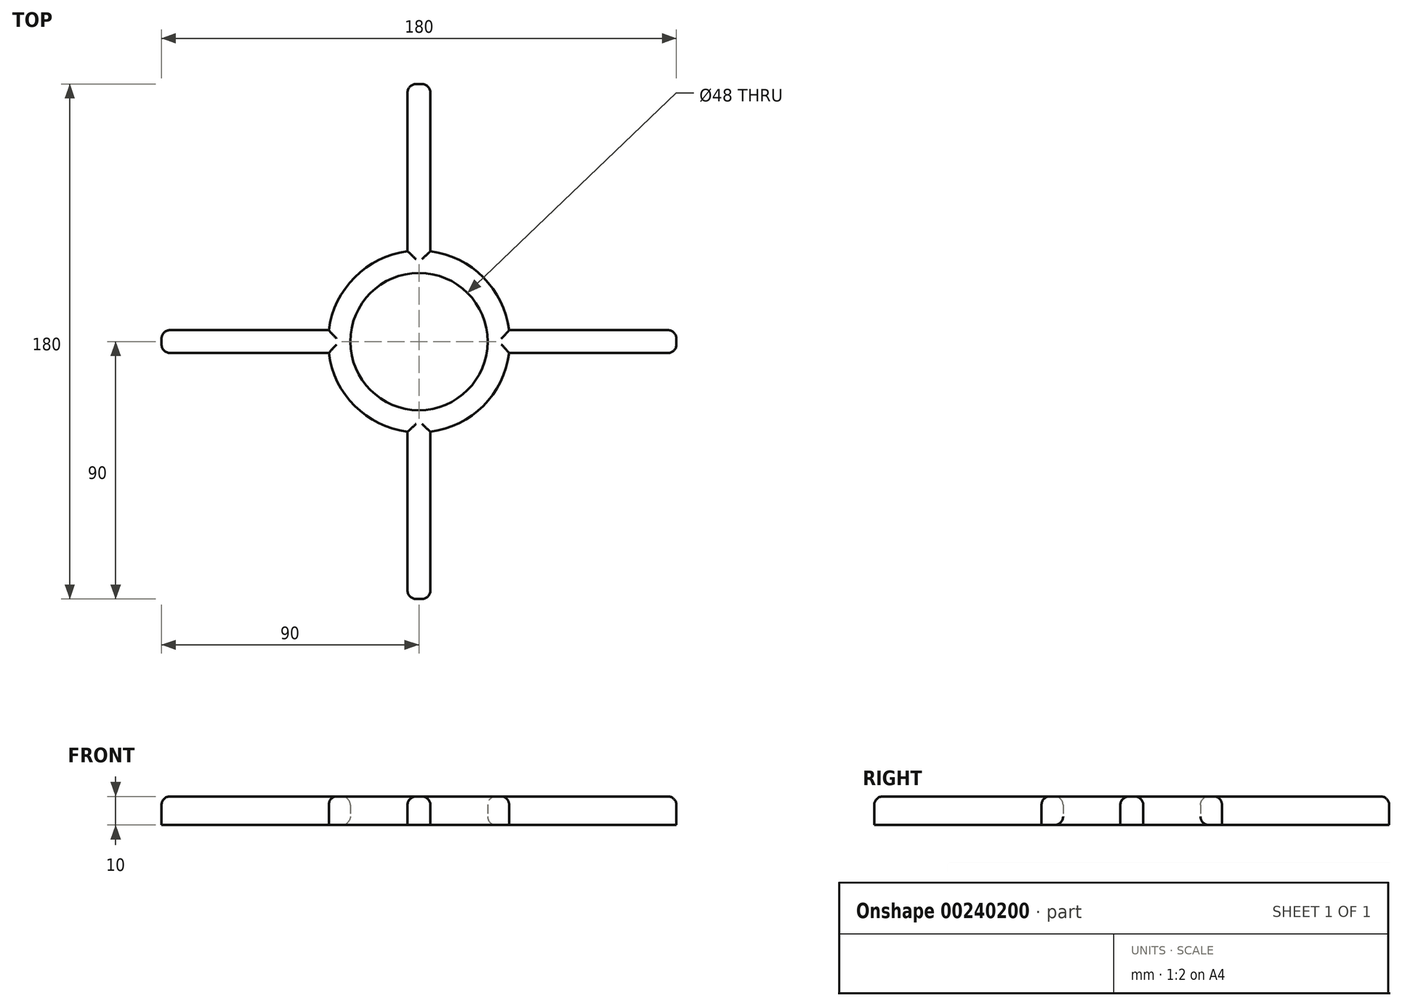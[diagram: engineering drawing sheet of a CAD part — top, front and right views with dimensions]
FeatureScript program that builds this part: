
annotation { "Feature Type Name" : "Feature", "Feature Type Description" : "" }
export const myFeature = defineFeature(function(context is Context, id is Id, definition is map)
    precondition{}
    {
        {
            var Q0;
            Q0=qCreatedBy(makeId("Top.planeOp"),FACE);
            var sketch = newSketch(context, id + "F0", { "sketchPlane" : qUnion([Q0])});
            skLineSegment(sketch, "E0.bottom", {"start": v(90, -4) * mm, "end": v(31.53, -4) * mm});
            skLineSegment(sketch, "E0.top", {"start": v(90, 4) * mm, "end": v(31.53, 4) * mm});
            skLineSegment(sketch, "E0.left", {"start": v(90, -4) * mm, "end": v(90, 4) * mm});
            skLineSegment(sketch, "E0.right", {"start": v(-90, -4) * mm, "end": v(-90, 4) * mm});
            skPoint(sketch, "E0.middle", {"position": v(0, 0) * mm});
            skCircle(sketch, "E1", {"center": v(0, 0) * mm, "radius": 24 * mm});
            skArc(sketch, "E2", {"start": v(-31.53, -4) * mm, "mid": v(-22.47, -22.47) * mm, "end": v(-4, -31.53) * mm});
            skArc(sketch, "E3.trimOffspring", {"start": v(31.53, 4) * mm, "mid": v(22.47, 22.47) * mm, "end": v(4, 31.53) * mm});
            skLineSegment(sketch, "E4.trimOffspring", {"start": v(-31.53, -4) * mm, "end": v(-90, -4) * mm});
            skLineSegment(sketch, "E5.trimOffspring", {"start": v(-31.53, 4) * mm, "end": v(-90, 4) * mm});
            skLineSegment(sketch, "E6.bottom", {"start": v(-4, 90) * mm, "end": v(4, 90) * mm});
            skLineSegment(sketch, "E6.top", {"start": v(-4, -90) * mm, "end": v(4, -90) * mm});
            skLineSegment(sketch, "E6.left", {"start": v(-4, 90) * mm, "end": v(-4, 31.53) * mm});
            skLineSegment(sketch, "E6.right", {"start": v(4, 90) * mm, "end": v(4, 31.53) * mm});
            skLineSegment(sketch, "E7.trimOffspring", {"start": v(-4, -31.53) * mm, "end": v(-4, -90) * mm});
            skLineSegment(sketch, "E8.trimOffspring", {"start": v(4, -31.53) * mm, "end": v(4, -90) * mm});
            skArc(sketch, "E9.trimOffspring", {"start": v(4, -31.53) * mm, "mid": v(22.47, -22.47) * mm, "end": v(31.53, -4) * mm});
            skArc(sketch, "E10.trimOffspring", {"start": v(-4, 31.53) * mm, "mid": v(-22.47, 22.47) * mm, "end": v(-31.53, 4) * mm});
            skSolve(sketch);
        }
        {
            var Q0;
            Q0=makeQuery(id+"F0.imprint","IMPRINT",FACE,{"disambiguationData":[TD([[makeQuery(id+"F0.imprint","IMPRINT",EDGE,{"derivedFrom":sQuery(id+"F0.wireOp",EDGE,"E0.bottom")}),-1.0]])]});
            extrude(context, id + "F1", {"entities" : qUnion([Q0]), "depth" : 10 * mm});
        }
        {
            var Q0;
            Q0=makeQuery(id+"F1.opExtrude","CAP_FACE",FACE,{"disambiguationData":[OSD([sQuery(id+"F0.wireOp",EDGE,"E0.bottom"),sQuery(id+"F0.wireOp",EDGE,"E0.top"),sQuery(id+"F0.wireOp",EDGE,"E0.left"),sQuery(id+"F0.wireOp",EDGE,"E0.right"),sQuery(id+"F0.wireOp",EDGE,"E1"),sQuery(id+"F0.wireOp",EDGE,"E2"),sQuery(id+"F0.wireOp",EDGE,"E3.trimOffspring"),sQuery(id+"F0.wireOp",EDGE,"E4.trimOffspring"),sQuery(id+"F0.wireOp",EDGE,"E5.trimOffspring"),sQuery(id+"F0.wireOp",EDGE,"E6.bottom"),sQuery(id+"F0.wireOp",EDGE,"E6.top"),sQuery(id+"F0.wireOp",EDGE,"E6.left"),sQuery(id+"F0.wireOp",EDGE,"E6.right"),sQuery(id+"F0.wireOp",EDGE,"E7.trimOffspring"),sQuery(id+"F0.wireOp",EDGE,"E8.trimOffspring"),sQuery(id+"F0.wireOp",EDGE,"E9.trimOffspring"),sQuery(id+"F0.wireOp",EDGE,"E10.trimOffspring")])],"isStart":false});
            fillet(context, id + "F2", {"entities" : qUnion([Q0]), "radius" : 3 * mm, "tangentPropagation" : true, "allowEdgeOverflow" : false});
        }
        {
            var Q0;
            Q0=makeQuery(id+"F1.opExtrude","SWEPT_EDGE",EDGE,{"disambiguationData":[OSD([sQuery(id+"F0.wireOp",EDGE,"E0.right"),sQuery(id+"F0.wireOp",EDGE,"E4.trimOffspring")])]});
            var Q1;
            Q1=makeQuery(id+"F1.opExtrude","SWEPT_EDGE",EDGE,{"disambiguationData":[OSD([sQuery(id+"F0.wireOp",EDGE,"E0.right"),sQuery(id+"F0.wireOp",EDGE,"E5.trimOffspring")])]});
            var Q2;
            Q2=makeQuery(id+"F1.opExtrude","SWEPT_EDGE",EDGE,{"disambiguationData":[OSD([sQuery(id+"F0.wireOp",EDGE,"E6.top"),sQuery(id+"F0.wireOp",EDGE,"E8.trimOffspring")])]});
            var Q3;
            Q3=makeQuery(id+"F1.opExtrude","SWEPT_EDGE",EDGE,{"disambiguationData":[OSD([sQuery(id+"F0.wireOp",EDGE,"E6.top"),sQuery(id+"F0.wireOp",EDGE,"E7.trimOffspring")])]});
            var Q4;
            Q4=makeQuery(id+"F1.opExtrude","SWEPT_EDGE",EDGE,{"disambiguationData":[OSD([sQuery(id+"F0.wireOp",EDGE,"E0.bottom"),sQuery(id+"F0.wireOp",EDGE,"E0.left")])]});
            var Q5;
            Q5=makeQuery(id+"F1.opExtrude","SWEPT_EDGE",EDGE,{"disambiguationData":[OSD([sQuery(id+"F0.wireOp",EDGE,"E0.top"),sQuery(id+"F0.wireOp",EDGE,"E0.left")])]});
            var Q6;
            Q6=makeQuery(id+"F1.opExtrude","SWEPT_EDGE",EDGE,{"disambiguationData":[OSD([sQuery(id+"F0.wireOp",EDGE,"E6.bottom"),sQuery(id+"F0.wireOp",EDGE,"E6.right")])]});
            var Q7;
            Q7=makeQuery(id+"F1.opExtrude","SWEPT_EDGE",EDGE,{"disambiguationData":[OSD([sQuery(id+"F0.wireOp",EDGE,"E6.bottom"),sQuery(id+"F0.wireOp",EDGE,"E6.left")])]});
            var Q8;
            Q8=makeQuery(id+"F1.opExtrude","CAP_EDGE",EDGE,{"disambiguationData":[OSD([sQuery(id+"F0.wireOp",EDGE,"E1")])],"isStart":true});
            fillet(context, id + "F3", {"entities" : qUnion([Q0, Q1, Q2, Q3, Q4, Q5, Q6, Q7, Q8]), "radius" : 3 * mm, "tangentPropagation" : true, "allowEdgeOverflow" : false});
        }
    });
